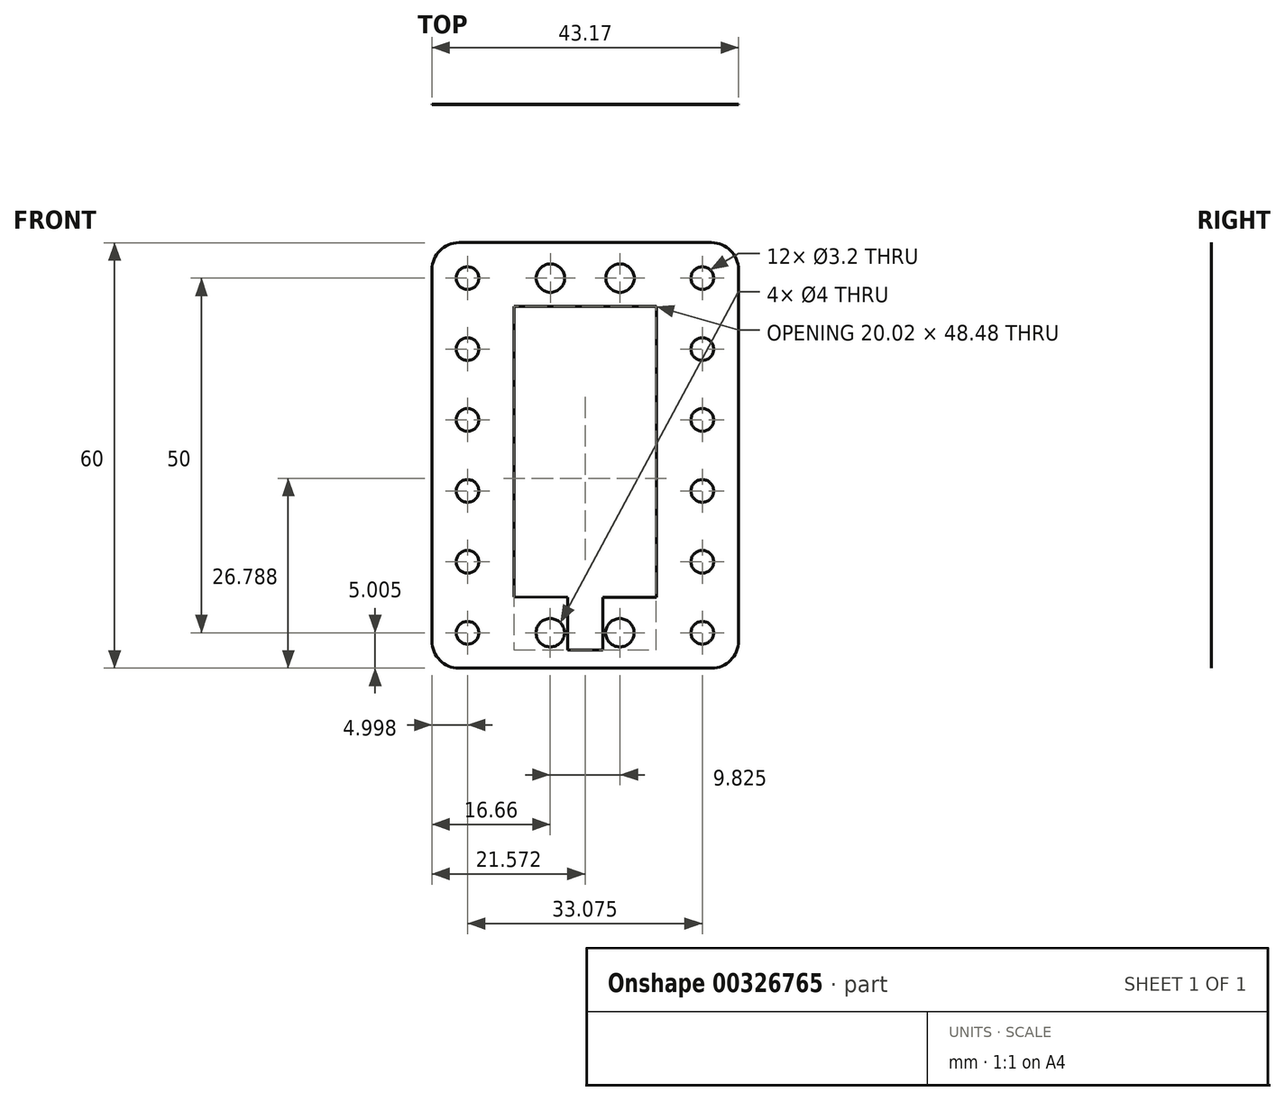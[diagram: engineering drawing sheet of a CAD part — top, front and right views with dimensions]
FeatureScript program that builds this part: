
annotation { "Feature Type Name" : "Feature", "Feature Type Description" : "" }
export const myFeature = defineFeature(function(context is Context, id is Id, definition is map)
    precondition{}
    {
        {
            var Q0;
            Q0=qCreatedBy(makeId("Front.planeOp"),FACE);
            var sketch = newSketch(context, id + "F0", { "sketchPlane" : qUnion([Q0])});
            skLineSegment(sketch, "E0.left", {"start": v(0, 0) * mm, "end": v(0, -41) * mm});
            skLineSegment(sketch, "E1.bottom", {"start": v(-7.75, 8.97) * mm, "end": v(27.8, 8.97) * mm});
            skLineSegment(sketch, "E1.top", {"start": v(-7.75, -51.02) * mm, "end": v(27.8, -51.02) * mm});
            skLineSegment(sketch, "E1.left", {"start": v(-11.56, 5.16) * mm, "end": v(-11.56, -47.22) * mm});
            skLineSegment(sketch, "E1.right", {"start": v(31.61, 5.16) * mm, "end": v(31.61, -47.22) * mm});
            skCircle(sketch, "E2", {"center": v(-6.56, 3.97) * mm, "radius": 1.6 * mm});
            skCircle(sketch, "E3.3.0.0", {"center": v(26.51, 3.97) * mm, "radius": 1.6 * mm});
            skLineSegment(sketch, "E3.direction1", {"start": v(-6.56, 3.97) * mm, "end": v(5.03, 3.97) * mm, "construction": true});
            skCircle(sketch, "E4.0.1.0", {"center": v(-6.56, -6.03) * mm, "radius": 1.6 * mm});
            skCircle(sketch, "E4.0.2.0", {"center": v(-6.56, -16.03) * mm, "radius": 1.6 * mm});
            skCircle(sketch, "E4.0.3.0", {"center": v(-6.56, -26.03) * mm, "radius": 1.6 * mm});
            skCircle(sketch, "E4.0.4.0", {"center": v(-6.56, -36.03) * mm, "radius": 1.6 * mm});
            skCircle(sketch, "E4.0.5.0", {"center": v(-6.56, -46.03) * mm, "radius": 1.6 * mm});
            skLineSegment(sketch, "E4.direction1", {"start": v(-6.56, 3.97) * mm, "end": v(20.38, 3.97) * mm, "construction": true});
            skLineSegment(sketch, "E4.direction2", {"start": v(-6.56, 3.97) * mm, "end": v(-6.56, -6.03) * mm, "construction": true});
            skCircle(sketch, "E5.0.1.0", {"center": v(26.51, -6.03) * mm, "radius": 1.6 * mm});
            skCircle(sketch, "E5.0.2.0", {"center": v(26.51, -16.03) * mm, "radius": 1.6 * mm});
            skCircle(sketch, "E5.0.3.0", {"center": v(26.51, -26.03) * mm, "radius": 1.6 * mm});
            skCircle(sketch, "E5.0.4.0", {"center": v(26.51, -36.03) * mm, "radius": 1.6 * mm});
            skCircle(sketch, "E5.0.5.0", {"center": v(26.51, -46.03) * mm, "radius": 1.6 * mm});
            skLineSegment(sketch, "E5.direction1", {"start": v(26.51, 3.97) * mm, "end": v(50.38, 3.97) * mm, "construction": true});
            skLineSegment(sketch, "E5.direction2", {"start": v(26.51, 3.97) * mm, "end": v(26.51, -6.03) * mm, "construction": true});
            skLineSegment(sketch, "E6.direction1", {"start": v(-6.56, -46.03) * mm, "end": v(5.03, -46.03) * mm, "construction": true});
            skCircle(sketch, "E7", {"center": v(5.13, 3.97) * mm, "radius": 2 * mm});
            skCircle(sketch, "E8", {"center": v(14.93, 3.97) * mm, "radius": 2 * mm});
            skCircle(sketch, "E9.MirrorC", {"center": v(5.1, -46.03) * mm, "radius": 2 * mm});
            skCircle(sketch, "E10.MirrorC", {"center": v(14.9, -46.03) * mm, "radius": 2 * mm});
            skLineSegment(sketch, "E11.top", {"start": v(7.52, -48.48) * mm, "end": v(12.47, -48.48) * mm});
            skLineSegment(sketch, "E11.left", {"start": v(7.52, -41.03) * mm, "end": v(7.52, -48.49) * mm});
            skLineSegment(sketch, "E11.right", {"start": v(12.47, -41.03) * mm, "end": v(12.47, -48.49) * mm});
            skPoint(sketch, "E12.visualSharp", {"position": v(-11.56, 8.97) * mm});
            skArc(sketch, "E12.filletArc", {"start": v(-7.75, 8.97) * mm, "mid": v(-10.45, 7.86) * mm, "end": v(-11.56, 5.16) * mm});
            skPoint(sketch, "E13.visualSharp", {"position": v(-11.56, -51.02) * mm});
            skArc(sketch, "E13.filletArc", {"start": v(-11.56, -47.22) * mm, "mid": v(-10.45, -49.9) * mm, "end": v(-7.75, -51.02) * mm});
            skPoint(sketch, "E14.visualSharp", {"position": v(31.61, -51.02) * mm});
            skArc(sketch, "E14.filletArc", {"start": v(27.8, -51.02) * mm, "mid": v(30.5, -49.9) * mm, "end": v(31.61, -47.22) * mm});
            skPoint(sketch, "E15.visualSharp", {"position": v(31.61, 8.97) * mm});
            skArc(sketch, "E15.filletArc", {"start": v(31.61, 5.16) * mm, "mid": v(30.5, 7.86) * mm, "end": v(27.8, 8.97) * mm});
            skLineSegment(sketch, "E16", {"start": v(0, 0) * mm, "end": v(20.03, 0) * mm});
            skLineSegment(sketch, "E17", {"start": v(20.03, 0) * mm, "end": v(20.03, -41.03) * mm});
            skLineSegment(sketch, "E18", {"start": v(0, -41) * mm, "end": v(7.52, -41.03) * mm});
            skLineSegment(sketch, "E19", {"start": v(12.47, -41.03) * mm, "end": v(20.03, -41.03) * mm});
            skSolve(sketch);
        }
        {
            var Q0;
            Q0=makeQuery(id+"F0.imprint","IMPRINT",FACE,{"disambiguationData":[TD([[makeQuery(id+"F0.imprint","IMPRINT",EDGE,{"derivedFrom":sQuery(id+"F0.wireOp",EDGE,"E0.left")}),-1.0]])]});
            extrude(context, id + "F1", {"entities" : qUnion([Q0]), "depth" : 1 / 203.2 * mm});
        }
    });
